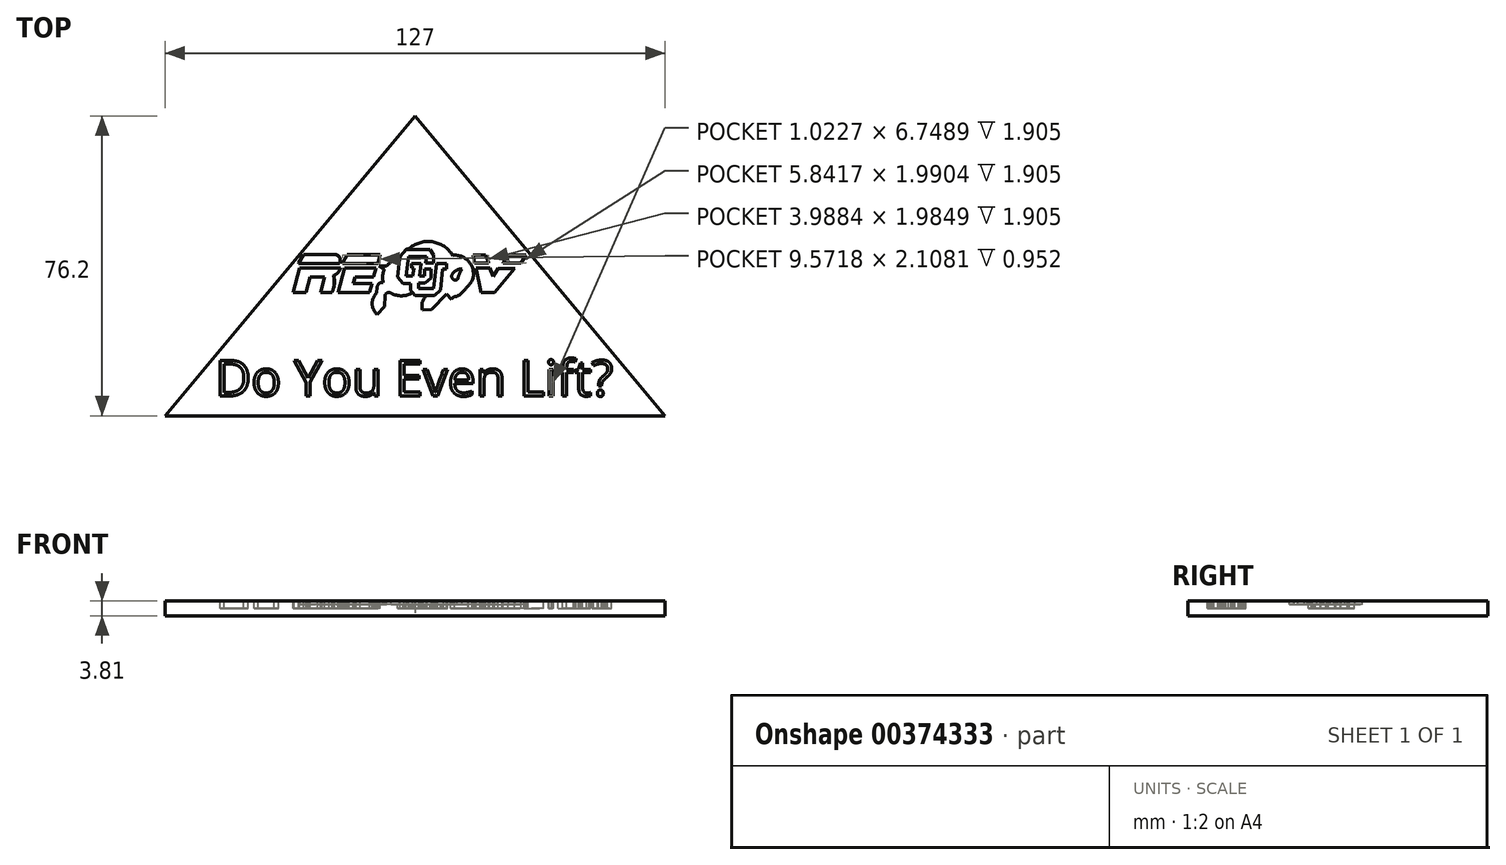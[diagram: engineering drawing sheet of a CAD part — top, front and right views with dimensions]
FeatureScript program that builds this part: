
annotation { "Feature Type Name" : "Feature", "Feature Type Description" : "" }
export const myFeature = defineFeature(function(context is Context, id is Id, definition is map)
    precondition{}
    {
        {
            var Q0;
            Q0=qCreatedBy(makeId("Top.planeOp"),FACE);
            var sketch = newSketch(context, id + "F0", { "sketchPlane" : qUnion([Q0])});
            skLineSegment(sketch, "E0", {"start": v(0, 76.2) * mm, "end": v(-63.5, 0) * mm});
            skLineSegment(sketch, "E1", {"start": v(-63.5, 0) * mm, "end": v(63.5, 0) * mm});
            skLineSegment(sketch, "E2", {"start": v(63.5, 0) * mm, "end": v(0, 76.2) * mm});
            skSolve(sketch);
        }
        {
            var Q0;
            Q0 = qSketchRegion(id + "F0", true);
            extrude(context, id + "F1", {"entities" : qUnion([Q0]), "depth" : 3.8 * mm});
        }
        {
            var Q0;
            Q0=makeQuery(id+"F1.opExtrude","CAP_FACE",FACE,{"disambiguationData":[OSD([sQuery(id+"F0.wireOp",EDGE,"E0"),sQuery(id+"F0.wireOp",EDGE,"E1"),sQuery(id+"F0.wireOp",EDGE,"E2")])],"isStart":false});
            var sketch = newSketch(context, id + "F2", { "sketchPlane" : qUnion([Q0])});
            skText(sketch, "E3", { "text": "Do You Even Lift?", "fontName": "OpenSans-Regular.ttf"});
            skLineSegment(sketch, "E4", {"start": v(-30.93, 31.35) * mm, "end": v(-29.27, 37.53) * mm});
            skLineSegment(sketch, "E5", {"start": v(-29.27, 37.53) * mm, "end": v(-18.93, 37.53) * mm});
            skLineSegment(sketch, "E6", {"start": v(-30.93, 31.35) * mm, "end": v(-27.7, 31.35) * mm});
            skLineSegment(sketch, "E7", {"start": v(-27.7, 31.35) * mm, "end": v(-26.66, 35.27) * mm});
            skLineSegment(sketch, "E8", {"start": v(-26.66, 35.27) * mm, "end": v(-22.92, 35.27) * mm});
            skLineSegment(sketch, "E9", {"start": v(-22.92, 35.27) * mm, "end": v(-23.97, 31.35) * mm});
            skLineSegment(sketch, "E10", {"start": v(-23.97, 31.35) * mm, "end": v(-21.1, 31.35) * mm});
            skLineSegment(sketch, "E11", {"start": v(-29.59, 38.76) * mm, "end": v(-19.22, 38.76) * mm});
            skLineSegment(sketch, "E12", {"start": v(-29.59, 38.76) * mm, "end": v(-28.34, 40.98) * mm});
            skLineSegment(sketch, "E13", {"start": v(-28.34, 40.98) * mm, "end": v(-20.47, 40.98) * mm});
            skLineSegment(sketch, "E14", {"start": v(-18.42, 38.76) * mm, "end": v(-17.23, 40.87) * mm});
            skLineSegment(sketch, "E15", {"start": v(-17.23, 40.87) * mm, "end": v(-8.85, 40.87) * mm});
            skLineSegment(sketch, "E16", {"start": v(-8.85, 40.87) * mm, "end": v(-9.41, 38.76) * mm});
            skLineSegment(sketch, "E17", {"start": v(-9.41, 38.76) * mm, "end": v(-18.42, 38.76) * mm});
            skLineSegment(sketch, "E18", {"start": v(-17.88, 37.53) * mm, "end": v(-19.53, 31.35) * mm});
            skLineSegment(sketch, "E19", {"start": v(-19.53, 31.35) * mm, "end": v(-11.51, 31.35) * mm});
            skLineSegment(sketch, "E20", {"start": v(-11.51, 31.35) * mm, "end": v(-10.9, 33.62) * mm});
            skLineSegment(sketch, "E21", {"start": v(-10.9, 33.62) * mm, "end": v(-15.69, 33.62) * mm});
            skLineSegment(sketch, "E22", {"start": v(-15.69, 33.62) * mm, "end": v(-15.23, 35.33) * mm});
            skLineSegment(sketch, "E23", {"start": v(-15.23, 35.33) * mm, "end": v(-10.53, 35.33) * mm});
            skLineSegment(sketch, "E24", {"start": v(-10.53, 35.33) * mm, "end": v(-9.94, 37.53) * mm});
            skLineSegment(sketch, "E25", {"start": v(-9.94, 37.53) * mm, "end": v(-17.88, 37.53) * mm});
            skLineSegment(sketch, "E26", {"start": v(15.53, 37.52) * mm, "end": v(16.77, 31.31) * mm});
            skLineSegment(sketch, "E27", {"start": v(16.77, 31.31) * mm, "end": v(20.24, 31.31) * mm});
            skLineSegment(sketch, "E28", {"start": v(20.24, 31.31) * mm, "end": v(25.36, 37.4) * mm});
            skLineSegment(sketch, "E29", {"start": v(25.36, 37.4) * mm, "end": v(21.09, 37.4) * mm});
            skLineSegment(sketch, "E30", {"start": v(21.09, 37.4) * mm, "end": v(19.8, 35.46) * mm});
            skLineSegment(sketch, "E31", {"start": v(19.8, 35.46) * mm, "end": v(19, 37.56) * mm});
            skLineSegment(sketch, "E32", {"start": v(19, 37.56) * mm, "end": v(15.53, 37.52) * mm});
            skLineSegment(sketch, "E33", {"start": v(18.7, 38.85) * mm, "end": v(17.95, 40.83) * mm});
            skLineSegment(sketch, "E34", {"start": v(17.95, 40.83) * mm, "end": v(14.72, 40.83) * mm});
            skLineSegment(sketch, "E35", {"start": v(14.72, 40.83) * mm, "end": v(15.12, 38.85) * mm});
            skLineSegment(sketch, "E36", {"start": v(15.12, 38.85) * mm, "end": v(18.7, 38.85) * mm});
            skLineSegment(sketch, "E37", {"start": v(22.37, 38.85) * mm, "end": v(23.7, 40.84) * mm});
            skLineSegment(sketch, "E38", {"start": v(23.7, 40.84) * mm, "end": v(28.22, 40.84) * mm});
            skLineSegment(sketch, "E39", {"start": v(28.22, 40.84) * mm, "end": v(26.89, 38.85) * mm});
            skLineSegment(sketch, "E40", {"start": v(26.89, 38.85) * mm, "end": v(22.37, 38.85) * mm});
            skLineSegment(sketch, "E41", {"start": v(2.67, 38.85) * mm, "end": v(4.78, 38.85) * mm});
            skLineSegment(sketch, "E42", {"start": v(4.78, 38.85) * mm, "end": v(4.78, 40.9) * mm});
            skLineSegment(sketch, "E43", {"start": v(4.78, 40.9) * mm, "end": v(3.87, 42.3) * mm});
            skLineSegment(sketch, "E44", {"start": v(3.87, 42.3) * mm, "end": v(-2.2, 42.3) * mm});
            skLineSegment(sketch, "E45", {"start": v(-2.2, 42.3) * mm, "end": v(-3.85, 40.47) * mm});
            skLineSegment(sketch, "E46", {"start": v(-3.85, 40.47) * mm, "end": v(-4.42, 35.28) * mm});
            skLineSegment(sketch, "E47", {"start": v(-4.42, 35.28) * mm, "end": v(-2.97, 33.66) * mm});
            skLineSegment(sketch, "E48", {"start": v(-2.97, 33.66) * mm, "end": v(-1.1, 33.66) * mm});
            skLineSegment(sketch, "E49", {"start": v(-1.1, 33.66) * mm, "end": v(-1.1, 31.8) * mm});
            skLineSegment(sketch, "E50", {"start": v(-1.1, 31.8) * mm, "end": v(0, 30.56) * mm});
            skLineSegment(sketch, "E51", {"start": v(0, 30.56) * mm, "end": v(4.98, 30.56) * mm});
            skLineSegment(sketch, "E52", {"start": v(4.98, 30.56) * mm, "end": v(6.49, 31.98) * mm});
            skLineSegment(sketch, "E53", {"start": v(6.49, 31.98) * mm, "end": v(7.03, 37.3) * mm});
            skLineSegment(sketch, "E54", {"start": v(7.03, 37.3) * mm, "end": v(8.02, 37.3) * mm});
            skLineSegment(sketch, "E55", {"start": v(8.02, 37.3) * mm, "end": v(8.02, 38.76) * mm});
            skLineSegment(sketch, "E56", {"start": v(8.02, 38.76) * mm, "end": v(5.43, 38.76) * mm});
            skLineSegment(sketch, "E57", {"start": v(5.43, 38.76) * mm, "end": v(4.66, 32.4) * mm});
            skLineSegment(sketch, "E58", {"start": v(4.66, 32.4) * mm, "end": v(0.93, 32.4) * mm});
            skLineSegment(sketch, "E59", {"start": v(0.93, 32.4) * mm, "end": v(0.93, 33.75) * mm});
            skLineSegment(sketch, "E60", {"start": v(0.93, 33.75) * mm, "end": v(2.55, 33.75) * mm});
            skLineSegment(sketch, "E61", {"start": v(2.55, 33.75) * mm, "end": v(4.12, 35.09) * mm});
            skLineSegment(sketch, "E62", {"start": v(4.12, 35.09) * mm, "end": v(4.12, 37.3) * mm});
            skLineSegment(sketch, "E63", {"start": v(4.12, 37.3) * mm, "end": v(2.44, 37.3) * mm});
            skLineSegment(sketch, "E64", {"start": v(2.44, 37.3) * mm, "end": v(2.44, 35.54) * mm});
            skLineSegment(sketch, "E65", {"start": v(2.44, 35.54) * mm, "end": v(1.22, 35.54) * mm});
            skLineSegment(sketch, "E66", {"start": v(1.22, 35.54) * mm, "end": v(1.53, 38.76) * mm});
            skLineSegment(sketch, "E67", {"start": v(1.53, 38.76) * mm, "end": v(-0.84, 38.76) * mm});
            skLineSegment(sketch, "E68", {"start": v(-0.84, 38.76) * mm, "end": v(-0.83, 37.52) * mm});
            skLineSegment(sketch, "E69", {"start": v(-0.83, 37.52) * mm, "end": v(-0.3, 37.52) * mm});
            skLineSegment(sketch, "E70", {"start": v(-0.3, 37.52) * mm, "end": v(-0.58, 35.54) * mm});
            skLineSegment(sketch, "E71", {"start": v(-0.58, 35.54) * mm, "end": v(-2.23, 35.54) * mm});
            skLineSegment(sketch, "E72", {"start": v(-2.23, 35.54) * mm, "end": v(-1.66, 40.53) * mm});
            skLineSegment(sketch, "E73", {"start": v(-1.66, 40.53) * mm, "end": v(2.95, 40.53) * mm});
            skLineSegment(sketch, "E74", {"start": v(2.95, 40.53) * mm, "end": v(2.67, 38.85) * mm});
            skArc(sketch, "E75", {"start": v(9.53, 40.72) * mm, "mid": v(4.28, 44.17) * mm, "end": v(-1.72, 42.3) * mm});
            skArc(sketch, "E76", {"start": v(14.49, 34.3) * mm, "mid": v(13.84, 38.93) * mm, "end": v(9.53, 40.72) * mm});
            skArc(sketch, "E77", {"start": v(10.7, 30.23) * mm, "mid": v(12.75, 32.12) * mm, "end": v(14.49, 34.3) * mm});
            skArc(sketch, "E78", {"start": v(-3.94, 39.73) * mm, "mid": v(-5.8, 39.22) * mm, "end": v(-7.27, 37.95) * mm});
            skArc(sketch, "E79", {"start": v(-7.86, 37.17) * mm, "mid": v(-8.25, 35.54) * mm, "end": v(-8.12, 33.87) * mm});
            skArc(sketch, "E80", {"start": v(-8.12, 33.87) * mm, "mid": v(-9.13, 33.56) * mm, "end": v(-9.66, 32.64) * mm});
            skArc(sketch, "E81", {"start": v(-6.09, 31.12) * mm, "mid": v(-7.02, 31.22) * mm, "end": v(-7.68, 30.55) * mm});
            skArc(sketch, "E82", {"start": v(-6.09, 31.12) * mm, "mid": v(-3.34, 30.43) * mm, "end": v(-0.65, 31.3) * mm});
            skArc(sketch, "E83", {"start": v(2.95, 30.56) * mm, "mid": v(1.83, 28.86) * mm, "end": v(1.9, 26.82) * mm});
            skArc(sketch, "E84", {"start": v(-9.8, 31.12) * mm, "mid": v(-10.92, 28.38) * mm, "end": v(-9.6, 25.72) * mm});
            skArc(sketch, "E85", {"start": v(10.7, 30.23) * mm, "mid": v(9.85, 30.13) * mm, "end": v(9.22, 29.55) * mm});
            skLineSegment(sketch, "E86", {"start": v(-9.6, 25.72) * mm, "end": v(-7.76, 27.78) * mm});
            skLineSegment(sketch, "E87", {"start": v(-7.76, 27.78) * mm, "end": v(-7.68, 30.55) * mm});
            skLineSegment(sketch, "E88", {"start": v(-9.8, 31.12) * mm, "end": v(-9.66, 32.64) * mm});
            skLineSegment(sketch, "E89", {"start": v(-7.86, 37.17) * mm, "end": v(-9.2, 38.03) * mm});
            skLineSegment(sketch, "E90", {"start": v(-9.2, 38.03) * mm, "end": v(-7.27, 37.95) * mm});
            skLineSegment(sketch, "E91", {"start": v(1.9, 26.82) * mm, "end": v(4.14, 27.02) * mm});
            skLineSegment(sketch, "E92", {"start": v(4.14, 27.02) * mm, "end": v(8.02, 30.87) * mm});
            skLineSegment(sketch, "E93", {"start": v(8.02, 30.87) * mm, "end": v(9.22, 29.55) * mm});
            skArc(sketch, "E94", {"start": v(9.54, 36.05) * mm, "mid": v(9.53, 34.76) * mm, "end": v(10.81, 34.66) * mm});
            skArc(sketch, "E95", {"start": v(11.88, 37.23) * mm, "mid": v(11.23, 36.02) * mm, "end": v(10.84, 34.7) * mm});
            skArc(sketch, "E96", {"start": v(11.88, 37.23) * mm, "mid": v(10.56, 36.95) * mm, "end": v(9.54, 36.05) * mm});
            skPoint(sketch, "E97.visualSharp", {"position": v(10.83, 34.68) * mm});
            skArc(sketch, "E97.filletArc", {"start": v(10.81, 34.66) * mm, "mid": v(10.83, 34.68) * mm, "end": v(10.84, 34.7) * mm});
            skArc(sketch, "E98", {"start": v(-20.73, 35.68) * mm, "mid": v(-19.6, 36.37) * mm, "end": v(-18.93, 37.53) * mm});
            skArc(sketch, "E99", {"start": v(-21.1, 31.35) * mm, "mid": v(-20.51, 33.48) * mm, "end": v(-20.73, 35.68) * mm});
            skArc(sketch, "E100", {"start": v(-19.22, 38.76) * mm, "mid": v(-19.2, 40.24) * mm, "end": v(-20.47, 40.98) * mm});
            const initialGuessF2  = {"E3": [-0.0508, 0.00508, 1, 0, 0.00908]};
            skSetInitialGuess(sketch, initialGuessF2);
            skSolve(sketch);
        }
        {
            var Q0;
            Q0=makeQuery(id+"F2.imprint","IMPRINT",FACE,{"disambiguationData":[TD([[makeQuery(id+"F2.imprint","IMPRINT",EDGE,{"derivedFrom":sQuery(id+"F2.wireOp",EDGE,"E4")}),-1.0]])]});
            var Q1;
            Q1=makeQuery(id+"F2.imprint","IMPRINT",FACE,{"disambiguationData":[TD([[makeQuery(id+"F2.imprint","IMPRINT",EDGE,{"derivedFrom":sQuery(id+"F2.wireOp",EDGE,"E11")}),1.0]])]});
            var Q2;
            Q2=makeQuery(id+"F2.imprint","IMPRINT",FACE,{"disambiguationData":[TD([[makeQuery(id+"F2.imprint","IMPRINT",EDGE,{"derivedFrom":sQuery(id+"F2.wireOp",EDGE,"E14")}),-1.0]])]});
            var Q3;
            Q3=makeQuery(id+"F2.imprint","IMPRINT",FACE,{"disambiguationData":[TD([[makeQuery(id+"F2.imprint","IMPRINT",EDGE,{"derivedFrom":sQuery(id+"F2.wireOp",EDGE,"E18")}),1.0]])]});
            var Q4;
            Q4=makeQuery(id+"F2.imprint","IMPRINT",FACE,{"disambiguationData":[TD([[makeQuery(id+"F2.imprint","IMPRINT",EDGE,{"derivedFrom":sQuery(id+"F2.wireOp",EDGE,"E26")}),1.0]])]});
            var Q5;
            Q5=makeQuery(id+"F2.imprint","IMPRINT",FACE,{"disambiguationData":[TD([[makeQuery(id+"F2.imprint","IMPRINT",EDGE,{"derivedFrom":sQuery(id+"F2.wireOp",EDGE,"E33")}),1.0]])]});
            var Q6;
            Q6=makeQuery(id+"F2.imprint","IMPRINT",FACE,{"disambiguationData":[TD([[makeQuery(id+"F2.imprint","IMPRINT",EDGE,{"derivedFrom":sQuery(id+"F2.wireOp",EDGE,"E37")}),-1.0]])]});
            var Q7;
            Q7=makeQuery(id+"F2.imprint","IMPRINT",FACE,{"disambiguationData":[TD([[makeQuery(id+"F2.imprint","IMPRINT",EDGE,{"derivedFrom":sQuery(id+"F2.wireOp",EDGE,"E41")}),1.0]])]});
            var Q8;
            Q8=makeQuery(id+"F2.imprint","IMPRINT",FACE,{"disambiguationData":[TD([[makeQuery(id+"F2.imprint","IMPRINT",EDGE,{"derivedFrom":sQuery(id+"F2.wireOp",EDGE,"E3.sketch_text.stroke-0")}),-1.0]])]});
            var Q9;
            Q9=makeQuery(id+"F2.imprint","IMPRINT",FACE,{"disambiguationData":[TD([[makeQuery(id+"F2.imprint","IMPRINT",EDGE,{"derivedFrom":sQuery(id+"F2.wireOp",EDGE,"E3.sketch_text.stroke-14")}),-1.0]])]});
            var Q10;
            Q10=makeQuery(id+"F2.imprint","IMPRINT",FACE,{"disambiguationData":[TD([[makeQuery(id+"F2.imprint","IMPRINT",EDGE,{"derivedFrom":sQuery(id+"F2.wireOp",EDGE,"E3.sketch_text.stroke-31")}),-1.0]])]});
            var Q11;
            Q11=makeQuery(id+"F2.imprint","IMPRINT",FACE,{"disambiguationData":[TD([[makeQuery(id+"F2.imprint","IMPRINT",EDGE,{"derivedFrom":sQuery(id+"F2.wireOp",EDGE,"E3.sketch_text.stroke-40")}),-1.0]])]});
            var Q12;
            Q12=makeQuery(id+"F2.imprint","IMPRINT",FACE,{"disambiguationData":[TD([[makeQuery(id+"F2.imprint","IMPRINT",EDGE,{"derivedFrom":sQuery(id+"F2.wireOp",EDGE,"E3.sketch_text.stroke-57")}),-1.0]])]});
            var Q13;
            Q13=makeQuery(id+"F2.imprint","IMPRINT",FACE,{"disambiguationData":[TD([[makeQuery(id+"F2.imprint","IMPRINT",EDGE,{"derivedFrom":sQuery(id+"F2.wireOp",EDGE,"E3.sketch_text.stroke-74")}),-1.0]])]});
            var Q14;
            Q14=makeQuery(id+"F2.imprint","IMPRINT",FACE,{"disambiguationData":[TD([[makeQuery(id+"F2.imprint","IMPRINT",EDGE,{"derivedFrom":sQuery(id+"F2.wireOp",EDGE,"E3.sketch_text.stroke-86")}),-1.0]])]});
            var Q15;
            Q15=makeQuery(id+"F2.imprint","IMPRINT",FACE,{"disambiguationData":[TD([[makeQuery(id+"F2.imprint","IMPRINT",EDGE,{"derivedFrom":sQuery(id+"F2.wireOp",EDGE,"E3.sketch_text.stroke-96")}),-1.0]])]});
            var Q16;
            Q16=makeQuery(id+"F2.imprint","IMPRINT",FACE,{"disambiguationData":[TD([[makeQuery(id+"F2.imprint","IMPRINT",EDGE,{"derivedFrom":sQuery(id+"F2.wireOp",EDGE,"E3.sketch_text.stroke-115")}),-1.0]])]});
            var Q17;
            Q17=makeQuery(id+"F2.imprint","IMPRINT",FACE,{"disambiguationData":[TD([[makeQuery(id+"F2.imprint","IMPRINT",EDGE,{"derivedFrom":sQuery(id+"F2.wireOp",EDGE,"E3.sketch_text.stroke-132")}),-1.0]])]});
            var Q18;
            Q18=makeQuery(id+"F2.imprint","IMPRINT",FACE,{"disambiguationData":[TD([[makeQuery(id+"F2.imprint","IMPRINT",EDGE,{"derivedFrom":sQuery(id+"F2.wireOp",EDGE,"E3.sketch_text.stroke-138")}),-1.0]])]});
            var Q19;
            Q19=makeQuery(id+"F2.imprint","IMPRINT",FACE,{"disambiguationData":[TD([[makeQuery(id+"F2.imprint","IMPRINT",EDGE,{"derivedFrom":sQuery(id+"F2.wireOp",EDGE,"E3.sketch_text.stroke-142")}),-1.0]])]});
            var Q20;
            Q20=makeQuery(id+"F2.imprint","IMPRINT",FACE,{"disambiguationData":[TD([[makeQuery(id+"F2.imprint","IMPRINT",EDGE,{"derivedFrom":sQuery(id+"F2.wireOp",EDGE,"E3.sketch_text.stroke-150")}),-1.0]])]});
            var Q21;
            Q21=makeQuery(id+"F2.imprint","IMPRINT",FACE,{"disambiguationData":[TD([[makeQuery(id+"F2.imprint","IMPRINT",EDGE,{"derivedFrom":sQuery(id+"F2.wireOp",EDGE,"E3.sketch_text.stroke-167")}),-1.0]])]});
            var Q22;
            Q22=makeQuery(id+"F2.imprint","IMPRINT",FACE,{"disambiguationData":[TD([[makeQuery(id+"F2.imprint","IMPRINT",EDGE,{"derivedFrom":sQuery(id+"F2.wireOp",EDGE,"E3.sketch_text.stroke-186")}),-1.0]])]});
            var Q23;
            Q23=makeQuery(id+"F2.imprint","IMPRINT",FACE,{"disambiguationData":[TD([[makeQuery(id+"F2.imprint","IMPRINT",EDGE,{"derivedFrom":sQuery(id+"F2.wireOp",EDGE,"E3.sketch_text.stroke-206")}),-1.0]])]});
            extrude(context, id + "F3", {"entities" : qUnion([Q0, Q1, Q2, Q3, Q4, Q5, Q6, Q7, Q8, Q9, Q10, Q11, Q12, Q13, Q14, Q15, Q16, Q17, Q18, Q19, Q20, Q21, Q22, Q23]), "operationType" : NewBodyOperationType.REMOVE, "oppositeDirection" : true, "depth" : 1.9 * mm});
        }
        {
            var Q0;
            {var subQ0=sQuery(id+"F0.wireOp",EDGE,"E0");var subQ1=sQuery(id+"F0.wireOp",EDGE,"E1");var subQ2=sQuery(id+"F0.wireOp",EDGE,"E2");Q0=makeQuery(id+"F3.boolean.opBoolean","SPLIT",FACE,{"disambiguationData":[TD([makeQuery(id+"F1.opExtrude","SWEPT_FACE",FACE,{"disambiguationData":[OSD([subQ0])]})])],"derivedFrom":makeQuery(id+"F1.opExtrude","CAP_FACE",FACE,{"disambiguationData":[OSD([subQ0,subQ1,subQ2])],"isStart":false})});}
            var sketch = newSketch(context, id + "F4", { "sketchPlane" : qUnion([Q0])});
            skLineSegment(sketch, "E101", {"start": v(-30.9, 31.42) * mm, "end": v(-29.24, 37.6) * mm});
            skLineSegment(sketch, "E102", {"start": v(-29.24, 37.6) * mm, "end": v(-18.9, 37.6) * mm});
            skLineSegment(sketch, "E103", {"start": v(-30.9, 31.42) * mm, "end": v(-27.67, 31.42) * mm});
            skLineSegment(sketch, "E104", {"start": v(-27.67, 31.42) * mm, "end": v(-26.62, 35.34) * mm});
            skLineSegment(sketch, "E105", {"start": v(-26.62, 35.34) * mm, "end": v(-22.89, 35.34) * mm});
            skLineSegment(sketch, "E106", {"start": v(-22.89, 35.34) * mm, "end": v(-23.94, 31.42) * mm});
            skLineSegment(sketch, "E107", {"start": v(-23.94, 31.42) * mm, "end": v(-21.06, 31.42) * mm});
            skLineSegment(sketch, "E108", {"start": v(-29.55, 38.84) * mm, "end": v(-19.18, 38.84) * mm});
            skLineSegment(sketch, "E109", {"start": v(-29.55, 38.84) * mm, "end": v(-28.3, 41.06) * mm});
            skLineSegment(sketch, "E110", {"start": v(-28.3, 41.06) * mm, "end": v(-20.44, 41.06) * mm});
            skLineSegment(sketch, "E111", {"start": v(-18.39, 38.84) * mm, "end": v(-17.19, 40.94) * mm});
            skLineSegment(sketch, "E112", {"start": v(-17.19, 40.94) * mm, "end": v(-8.81, 40.94) * mm});
            skLineSegment(sketch, "E113", {"start": v(-8.81, 40.94) * mm, "end": v(-9.38, 38.84) * mm});
            skLineSegment(sketch, "E114", {"start": v(-9.38, 38.84) * mm, "end": v(-18.39, 38.84) * mm});
            skLineSegment(sketch, "E115", {"start": v(-17.84, 37.6) * mm, "end": v(-19.5, 31.42) * mm});
            skLineSegment(sketch, "E116", {"start": v(-19.5, 31.42) * mm, "end": v(-11.48, 31.42) * mm});
            skLineSegment(sketch, "E117", {"start": v(-11.48, 31.42) * mm, "end": v(-10.87, 33.7) * mm});
            skLineSegment(sketch, "E118", {"start": v(-10.87, 33.7) * mm, "end": v(-15.65, 33.7) * mm});
            skLineSegment(sketch, "E119", {"start": v(-15.65, 33.7) * mm, "end": v(-15.2, 35.4) * mm});
            skLineSegment(sketch, "E120", {"start": v(-15.2, 35.4) * mm, "end": v(-10.5, 35.4) * mm});
            skLineSegment(sketch, "E121", {"start": v(-10.5, 35.4) * mm, "end": v(-9.9, 37.6) * mm});
            skLineSegment(sketch, "E122", {"start": v(-9.9, 37.6) * mm, "end": v(-17.84, 37.6) * mm});
            skLineSegment(sketch, "E123", {"start": v(15.56, 37.6) * mm, "end": v(16.81, 31.39) * mm});
            skLineSegment(sketch, "E124", {"start": v(16.81, 31.39) * mm, "end": v(20.28, 31.39) * mm});
            skLineSegment(sketch, "E125", {"start": v(20.28, 31.39) * mm, "end": v(25.4, 37.47) * mm});
            skLineSegment(sketch, "E126", {"start": v(25.4, 37.47) * mm, "end": v(21.12, 37.47) * mm});
            skLineSegment(sketch, "E127", {"start": v(21.12, 37.47) * mm, "end": v(19.83, 35.54) * mm});
            skLineSegment(sketch, "E128", {"start": v(19.83, 35.54) * mm, "end": v(19.03, 37.63) * mm});
            skLineSegment(sketch, "E129", {"start": v(19.03, 37.63) * mm, "end": v(15.56, 37.6) * mm});
            skLineSegment(sketch, "E130", {"start": v(18.74, 38.92) * mm, "end": v(17.98, 40.9) * mm});
            skLineSegment(sketch, "E131", {"start": v(17.98, 40.9) * mm, "end": v(14.76, 40.9) * mm});
            skLineSegment(sketch, "E132", {"start": v(14.76, 40.9) * mm, "end": v(15.16, 38.92) * mm});
            skLineSegment(sketch, "E133", {"start": v(15.16, 38.92) * mm, "end": v(18.74, 38.92) * mm});
            skLineSegment(sketch, "E134", {"start": v(22.41, 38.92) * mm, "end": v(23.74, 40.91) * mm});
            skLineSegment(sketch, "E135", {"start": v(23.74, 40.91) * mm, "end": v(28.25, 40.91) * mm});
            skLineSegment(sketch, "E136", {"start": v(28.25, 40.91) * mm, "end": v(26.93, 38.92) * mm});
            skLineSegment(sketch, "E137", {"start": v(26.93, 38.92) * mm, "end": v(22.41, 38.92) * mm});
            skLineSegment(sketch, "E138", {"start": v(2.7, 38.92) * mm, "end": v(4.81, 38.92) * mm});
            skLineSegment(sketch, "E139", {"start": v(4.81, 38.92) * mm, "end": v(4.81, 40.97) * mm});
            skLineSegment(sketch, "E140", {"start": v(4.81, 40.97) * mm, "end": v(3.9, 42.37) * mm});
            skLineSegment(sketch, "E141", {"start": v(3.9, 42.37) * mm, "end": v(-2.17, 42.37) * mm});
            skLineSegment(sketch, "E142", {"start": v(-2.17, 42.37) * mm, "end": v(-3.82, 40.54) * mm});
            skLineSegment(sketch, "E143", {"start": v(-3.82, 40.54) * mm, "end": v(-4.39, 35.36) * mm});
            skLineSegment(sketch, "E144", {"start": v(-4.39, 35.36) * mm, "end": v(-2.94, 33.74) * mm});
            skLineSegment(sketch, "E145", {"start": v(-2.94, 33.74) * mm, "end": v(-1.06, 33.74) * mm});
            skLineSegment(sketch, "E146", {"start": v(-1.06, 33.74) * mm, "end": v(-1.06, 31.88) * mm});
            skLineSegment(sketch, "E147", {"start": v(-1.06, 31.88) * mm, "end": v(0.04, 30.63) * mm});
            skLineSegment(sketch, "E148", {"start": v(0.04, 30.63) * mm, "end": v(5.01, 30.63) * mm});
            skLineSegment(sketch, "E149", {"start": v(5.01, 30.63) * mm, "end": v(6.52, 32.06) * mm});
            skLineSegment(sketch, "E150", {"start": v(6.52, 32.06) * mm, "end": v(7.06, 37.38) * mm});
            skLineSegment(sketch, "E151", {"start": v(7.06, 37.38) * mm, "end": v(8.06, 37.38) * mm});
            skLineSegment(sketch, "E152", {"start": v(8.06, 37.38) * mm, "end": v(8.06, 38.84) * mm});
            skLineSegment(sketch, "E153", {"start": v(8.06, 38.84) * mm, "end": v(5.47, 38.84) * mm});
            skLineSegment(sketch, "E154", {"start": v(5.47, 38.84) * mm, "end": v(4.7, 32.48) * mm});
            skLineSegment(sketch, "E155", {"start": v(4.7, 32.48) * mm, "end": v(0.97, 32.48) * mm});
            skLineSegment(sketch, "E156", {"start": v(0.97, 32.48) * mm, "end": v(0.97, 33.82) * mm});
            skLineSegment(sketch, "E157", {"start": v(0.97, 33.82) * mm, "end": v(2.6, 33.82) * mm});
            skLineSegment(sketch, "E158", {"start": v(2.6, 33.82) * mm, "end": v(4.16, 35.16) * mm});
            skLineSegment(sketch, "E159", {"start": v(4.16, 35.16) * mm, "end": v(4.16, 37.38) * mm});
            skLineSegment(sketch, "E160", {"start": v(4.16, 37.38) * mm, "end": v(2.48, 37.38) * mm});
            skLineSegment(sketch, "E161", {"start": v(2.48, 37.38) * mm, "end": v(2.48, 35.62) * mm});
            skLineSegment(sketch, "E162", {"start": v(2.48, 35.62) * mm, "end": v(1.25, 35.62) * mm});
            skLineSegment(sketch, "E163", {"start": v(1.25, 35.62) * mm, "end": v(1.56, 38.84) * mm});
            skLineSegment(sketch, "E164", {"start": v(1.56, 38.84) * mm, "end": v(-0.8, 38.84) * mm});
            skLineSegment(sketch, "E165", {"start": v(-0.8, 38.84) * mm, "end": v(-0.8, 37.6) * mm});
            skLineSegment(sketch, "E166", {"start": v(-0.8, 37.6) * mm, "end": v(-0.26, 37.6) * mm});
            skLineSegment(sketch, "E167", {"start": v(-0.26, 37.6) * mm, "end": v(-0.54, 35.62) * mm});
            skLineSegment(sketch, "E168", {"start": v(-0.54, 35.62) * mm, "end": v(-2.2, 35.62) * mm});
            skLineSegment(sketch, "E169", {"start": v(-2.2, 35.62) * mm, "end": v(-1.63, 40.6) * mm});
            skLineSegment(sketch, "E170", {"start": v(-1.63, 40.6) * mm, "end": v(2.99, 40.6) * mm});
            skLineSegment(sketch, "E171", {"start": v(2.99, 40.6) * mm, "end": v(2.7, 38.92) * mm});
            skArc(sketch, "E172", {"start": v(9.56, 40.8) * mm, "mid": v(4.31, 44.25) * mm, "end": v(-1.69, 42.37) * mm});
            skArc(sketch, "E173", {"start": v(14.52, 34.38) * mm, "mid": v(13.87, 39) * mm, "end": v(9.56, 40.8) * mm});
            skArc(sketch, "E174", {"start": v(10.73, 30.3) * mm, "mid": v(12.79, 32.2) * mm, "end": v(14.52, 34.38) * mm});
            skArc(sketch, "E175", {"start": v(-3.9, 39.8) * mm, "mid": v(-5.77, 39.3) * mm, "end": v(-7.23, 38.03) * mm});
            skArc(sketch, "E176", {"start": v(-7.83, 37.25) * mm, "mid": v(-8.21, 35.61) * mm, "end": v(-8.08, 33.94) * mm});
            skArc(sketch, "E177", {"start": v(-8.08, 33.94) * mm, "mid": v(-9.1, 33.63) * mm, "end": v(-9.62, 32.72) * mm});
            skArc(sketch, "E178", {"start": v(-6.05, 31.2) * mm, "mid": v(-6.98, 31.3) * mm, "end": v(-7.65, 30.63) * mm});
            skArc(sketch, "E179", {"start": v(-6.05, 31.2) * mm, "mid": v(-3.3, 30.5) * mm, "end": v(-0.61, 31.37) * mm});
            skArc(sketch, "E180", {"start": v(2.99, 30.63) * mm, "mid": v(1.87, 28.93) * mm, "end": v(1.93, 26.9) * mm});
            skArc(sketch, "E181", {"start": v(-9.76, 31.2) * mm, "mid": v(-10.89, 28.45) * mm, "end": v(-9.57, 25.8) * mm});
            skArc(sketch, "E182", {"start": v(10.73, 30.3) * mm, "mid": v(9.89, 30.2) * mm, "end": v(9.26, 29.63) * mm});
            skLineSegment(sketch, "E183", {"start": v(-9.57, 25.8) * mm, "end": v(-7.73, 27.86) * mm});
            skLineSegment(sketch, "E184", {"start": v(-7.73, 27.86) * mm, "end": v(-7.65, 30.63) * mm});
            skLineSegment(sketch, "E185", {"start": v(-9.76, 31.2) * mm, "end": v(-9.62, 32.72) * mm});
            skLineSegment(sketch, "E186", {"start": v(-7.83, 37.25) * mm, "end": v(-9.16, 38.1) * mm});
            skLineSegment(sketch, "E187", {"start": v(-9.16, 38.1) * mm, "end": v(-7.23, 38.03) * mm});
            skLineSegment(sketch, "E188", {"start": v(1.93, 26.9) * mm, "end": v(4.18, 27.09) * mm});
            skLineSegment(sketch, "E189", {"start": v(4.18, 27.09) * mm, "end": v(8.06, 30.95) * mm});
            skLineSegment(sketch, "E190", {"start": v(8.06, 30.95) * mm, "end": v(9.26, 29.63) * mm});
            skArc(sketch, "E191", {"start": v(9.58, 36.12) * mm, "mid": v(9.57, 34.84) * mm, "end": v(10.85, 34.74) * mm});
            skArc(sketch, "E192", {"start": v(11.92, 37.3) * mm, "mid": v(11.26, 36.1) * mm, "end": v(10.87, 34.77) * mm});
            skArc(sketch, "E193", {"start": v(11.92, 37.3) * mm, "mid": v(10.6, 37.03) * mm, "end": v(9.58, 36.12) * mm});
            skPoint(sketch, "E194.visualSharp", {"position": v(10.87, 34.75) * mm});
            skArc(sketch, "E194.filletArc", {"start": v(10.85, 34.74) * mm, "mid": v(10.86, 34.75) * mm, "end": v(10.87, 34.77) * mm});
            skArc(sketch, "E195", {"start": v(-20.7, 35.76) * mm, "mid": v(-19.56, 36.45) * mm, "end": v(-18.9, 37.6) * mm});
            skArc(sketch, "E196", {"start": v(-21.06, 31.42) * mm, "mid": v(-20.48, 33.55) * mm, "end": v(-20.7, 35.76) * mm});
            skArc(sketch, "E197", {"start": v(-19.18, 38.84) * mm, "mid": v(-19.16, 40.31) * mm, "end": v(-20.44, 41.06) * mm});
            skSolve(sketch);
        }
        {
            var Q0;
            Q0 = qSketchRegion(id + "F4", true);
            extrude(context, id + "F5", {"entities" : qUnion([Q0]), "operationType" : NewBodyOperationType.REMOVE, "oppositeDirection" : true, "depth" : 0.95 * mm});
        }
    });
